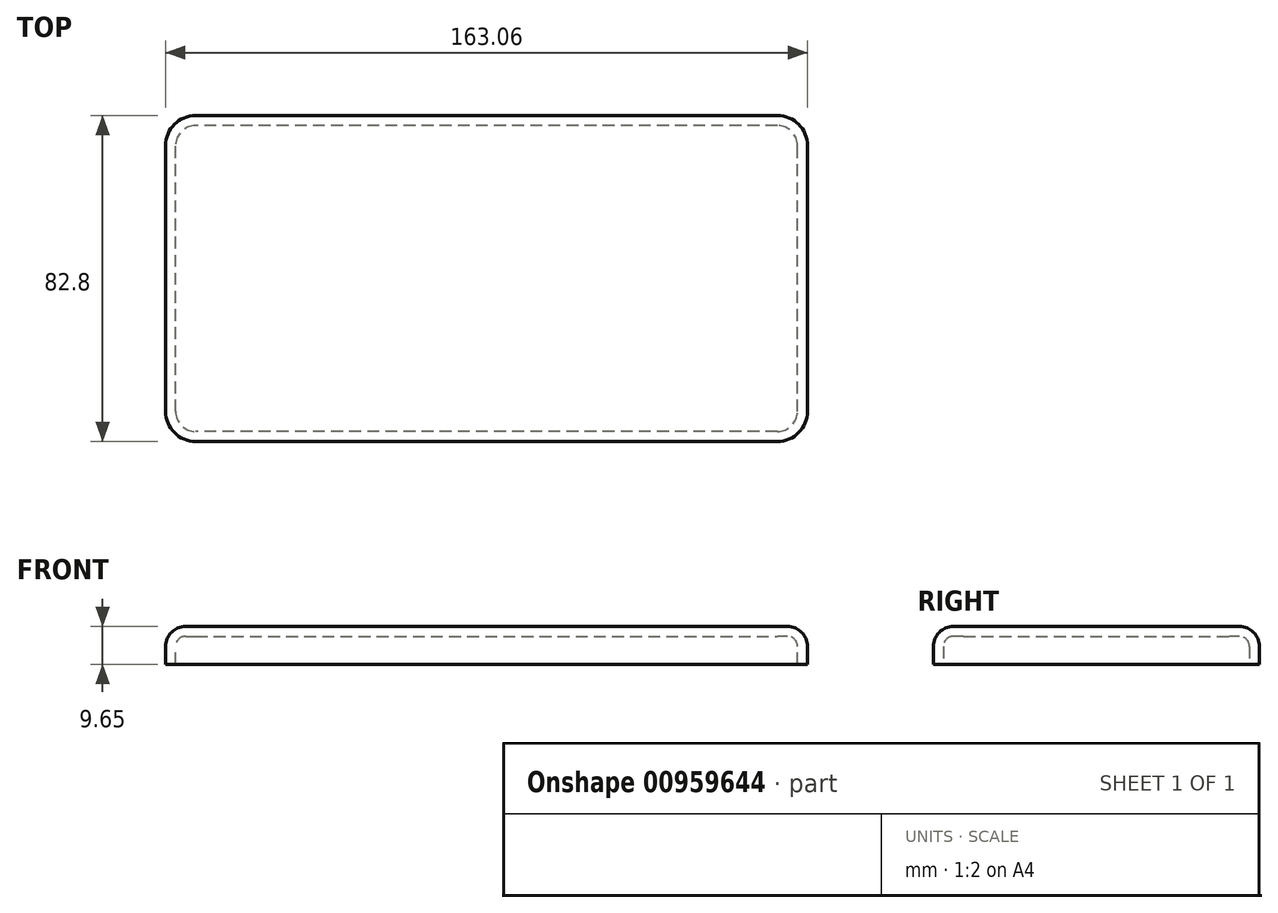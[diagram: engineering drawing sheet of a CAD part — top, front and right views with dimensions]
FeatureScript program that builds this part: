
annotation { "Feature Type Name" : "Feature", "Feature Type Description" : "" }
export const myFeature = defineFeature(function(context is Context, id is Id, definition is map)
    precondition{}
    {
        {
            var Q0;
            Q0=qCreatedBy(makeId("Top.planeOp"),FACE);
            var sketch = newSketch(context, id + "F0", { "sketchPlane" : qUnion([Q0])});
            skLineSegment(sketch, "E0.bottom", {"start": v(81.53, -41.4) * mm, "end": v(-81.53, -41.4) * mm});
            skLineSegment(sketch, "E0.top", {"start": v(81.53, 41.4) * mm, "end": v(-81.53, 41.4) * mm});
            skLineSegment(sketch, "E0.left", {"start": v(81.53, -41.4) * mm, "end": v(81.53, 41.4) * mm});
            skLineSegment(sketch, "E0.right", {"start": v(-81.53, -41.4) * mm, "end": v(-81.53, 41.4) * mm});
            skPoint(sketch, "E0.middle", {"position": v(0, 0) * mm});
            skSolve(sketch);
        }
        {
            var Q0;
            Q0 = qSketchRegion(id + "F0", true);
            extrude(context, id + "F1", {"entities" : qUnion([Q0]), "depth" : 9.65 * mm, "offsetDistance" : 25.4 * mm});
        }
        {
            var Q0;
            Q0=makeQuery(id+"F1.opExtrude","SWEPT_EDGE",EDGE,{"disambiguationData":[OSD([sQuery(id+"F0.wireOp",EDGE,"E0.top"),sQuery(id+"F0.wireOp",EDGE,"E0.right")])]});
            var Q1;
            Q1=makeQuery(id+"F1.opExtrude","SWEPT_EDGE",EDGE,{"disambiguationData":[OSD([sQuery(id+"F0.wireOp",EDGE,"E0.bottom"),sQuery(id+"F0.wireOp",EDGE,"E0.right")])]});
            var Q2;
            Q2=makeQuery(id+"F1.opExtrude","SWEPT_EDGE",EDGE,{"disambiguationData":[OSD([sQuery(id+"F0.wireOp",EDGE,"E0.top"),sQuery(id+"F0.wireOp",EDGE,"E0.left")])]});
            var Q3;
            Q3=makeQuery(id+"F1.opExtrude","SWEPT_EDGE",EDGE,{"disambiguationData":[OSD([sQuery(id+"F0.wireOp",EDGE,"E0.bottom"),sQuery(id+"F0.wireOp",EDGE,"E0.left")])]});
            fillet(context, id + "F2", {"entities" : qUnion([Q0, Q1, Q2, Q3]), "radius" : 7.62 * mm, "tangentPropagation" : true, "allowEdgeOverflow" : false});
        }
        {
            var Q0;
            Q0=makeQuery(id+"F1.opExtrude","CAP_FACE",FACE,{"disambiguationData":[OSD([sQuery(id+"F0.wireOp",EDGE,"E0.bottom"),sQuery(id+"F0.wireOp",EDGE,"E0.top"),sQuery(id+"F0.wireOp",EDGE,"E0.left"),sQuery(id+"F0.wireOp",EDGE,"E0.right")])],"isStart":false});
            fillet(context, id + "F3", {"entities" : qUnion([Q0]), "radius" : 5.08 * mm, "tangentPropagation" : true, "allowEdgeOverflow" : false});
        }
        {
            var Q0;
            Q0=makeQuery(id+"F1.opExtrude","CAP_FACE",FACE,{"disambiguationData":[OSD([sQuery(id+"F0.wireOp",EDGE,"E0.bottom"),sQuery(id+"F0.wireOp",EDGE,"E0.top"),sQuery(id+"F0.wireOp",EDGE,"E0.left"),sQuery(id+"F0.wireOp",EDGE,"E0.right")])],"isStart":true});
            shell(context, id + "F4", {"entities" : qUnion([Q0]), "thickness" : 2.54 * mm});
        }
    });
